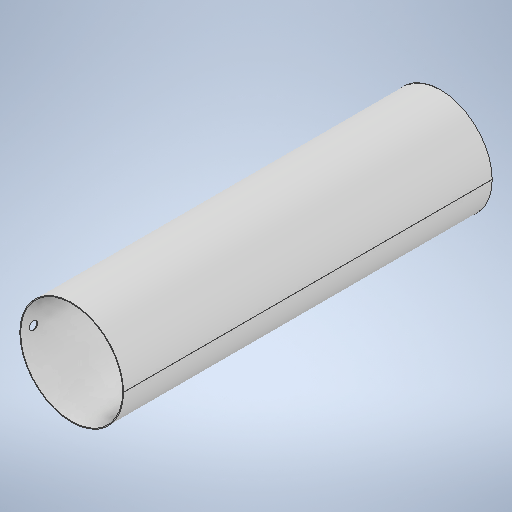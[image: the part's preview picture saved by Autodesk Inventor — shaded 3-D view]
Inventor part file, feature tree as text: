
AUTODESK INVENTOR PART (.ipt)
format: ipt  version: 2025 (Build 290162010, 162A)  size: 288,256 bytes
history: native  units: mm
features: other x2, sketch x2, revolve x1, extrude x1
ambient origin geometry x8: Origin, YZ Plane, XZ Plane, XY Plane, X Axis, Y Axis, Z Axis, Center Point
bodies: Solid1 (feature_tree)
feature tree (6):
  revolve  "Revolution1"  [1 undecoded]
  extrude  "Extrusion1"  Depth=100.0mm
  other  "A-Side Definition"
  sketch  "Sketch1"  dims[d0=6.0mm d1=2887.0mm]
  sketch  "Sketch2"  dims[d2=400.0mm d3=62.8144mm d4=65.0mm d5=100.0mm d6=0.0mm d7=0.0mm]
  other  "Definition1"
note: 1 required parameter value undecoded (feature->parameter linkage not recoverable at this tier; creation-order binding heuristic only, values carry confidence <= 0.55)
